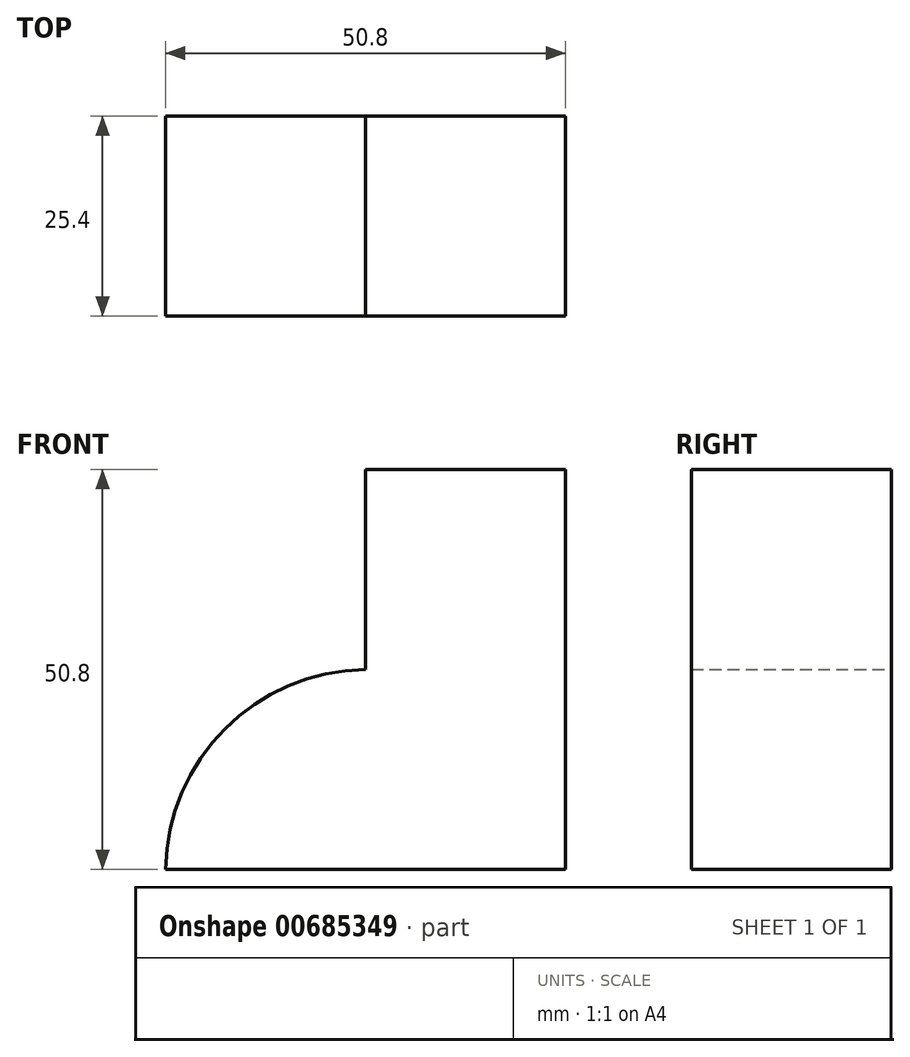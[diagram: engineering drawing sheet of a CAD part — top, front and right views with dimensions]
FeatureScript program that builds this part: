
annotation { "Feature Type Name" : "Feature", "Feature Type Description" : "" }
export const myFeature = defineFeature(function(context is Context, id is Id, definition is map)
    precondition{}
    {
        {
            var Q0;
            Q0=qCreatedBy(makeId("Front.planeOp"),FACE);
            var sketch = newSketch(context, id + "F0", { "sketchPlane" : qUnion([Q0])});
            skLineSegment(sketch, "E0", {"start": v(0, 0) * mm, "end": v(0, 25.4) * mm});
            skLineSegment(sketch, "E1", {"start": v(0, 25.4) * mm, "end": v(25.4, 25.4) * mm});
            skLineSegment(sketch, "E2", {"start": v(25.4, 25.4) * mm, "end": v(25.4, -25.4) * mm});
            skLineSegment(sketch, "E3", {"start": v(25.4, -25.4) * mm, "end": v(-25.4, -25.4) * mm});
            skArc(sketch, "E4", {"start": v(0, 0) * mm, "mid": v(-17.86, -7.54) * mm, "end": v(-25.4, -25.4) * mm});
            skSolve(sketch);
        }
        {
            var Q0;
            Q0=makeQuery(id+"F0.imprint","IMPRINT",FACE,{"disambiguationData":[TD([[makeQuery(id+"F0.imprint","IMPRINT",EDGE,{"derivedFrom":sQuery(id+"F0.wireOp",EDGE,"E0")}),-1.0]])]});
            extrude(context, id + "F1", {"entities" : qUnion([Q0]), "depth" : 25.4 * mm, "offsetDistance" : 25.4 * mm});
        }
    });
